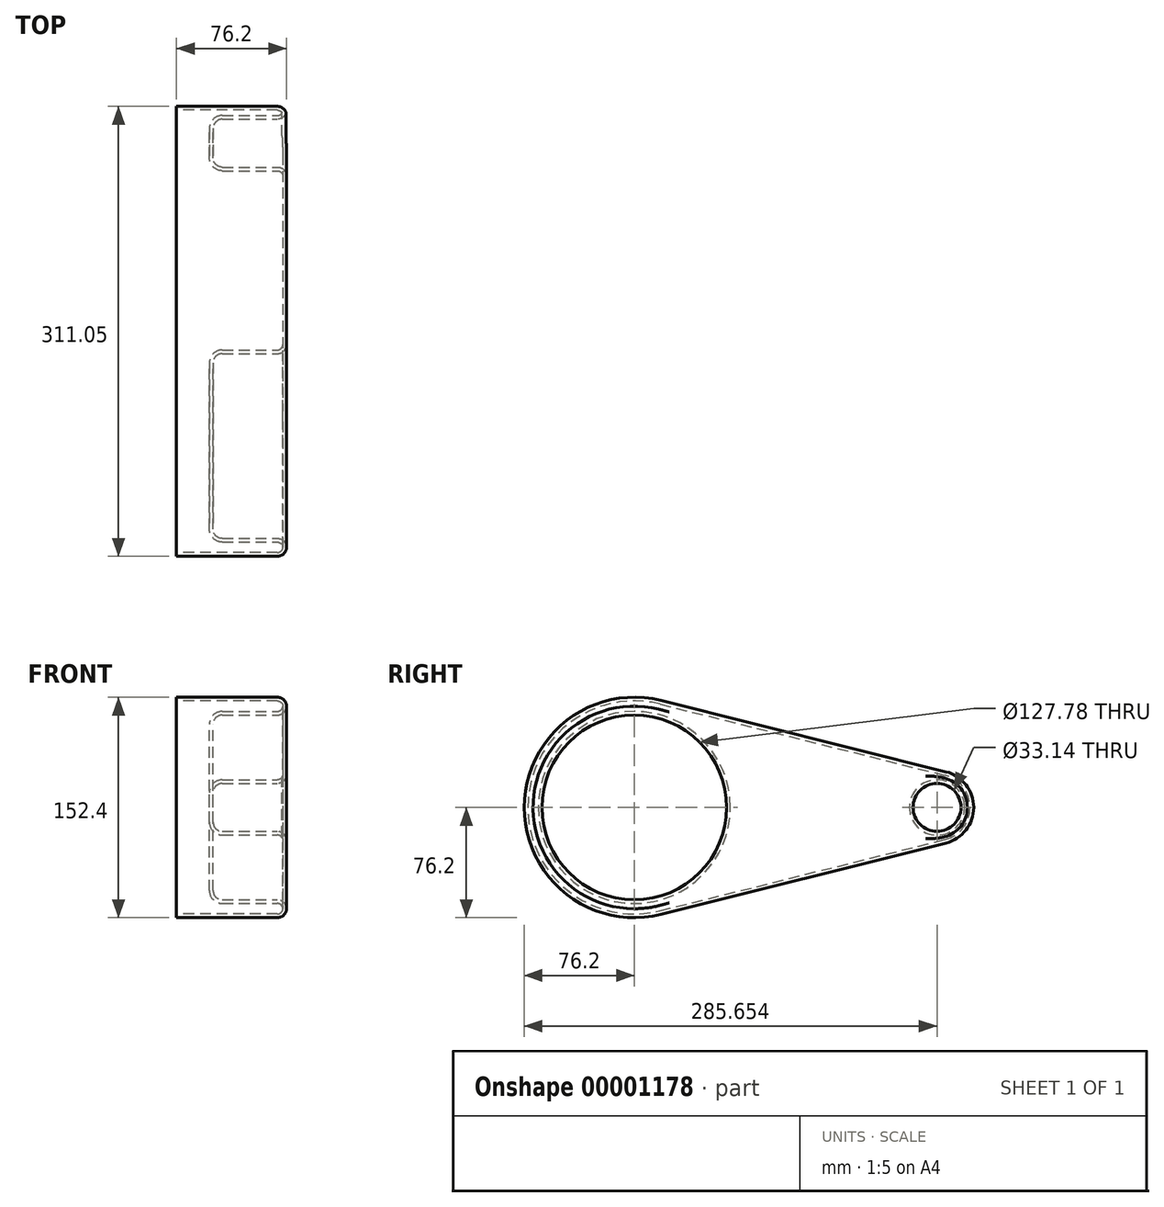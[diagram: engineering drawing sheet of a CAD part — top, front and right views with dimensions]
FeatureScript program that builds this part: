
annotation { "Feature Type Name" : "Feature", "Feature Type Description" : "" }
export const myFeature = defineFeature(function(context is Context, id is Id, definition is map)
    precondition{}
    {
        {
            var Q0;
            Q0=qCreatedBy(makeId("Right.planeOp"),FACE);
            var sketch = newSketch(context, id + "F0", { "sketchPlane" : qUnion([Q0])});
            skCircle(sketch, "E0", {"center": v(0, 0) * mm, "radius": 76.2 * mm});
            skCircle(sketch, "E1", {"center": v(209.45, 0) * mm, "radius": 25.4 * mm});
            skLineSegment(sketch, "E2", {"start": v(18.48, 73.92) * mm, "end": v(215.61, 24.64) * mm});
            skLineSegment(sketch, "E3", {"start": v(18.48, -73.92) * mm, "end": v(215.61, -24.64) * mm});
            skSolve(sketch);
        }
        {
            var Q0;
            {var subQ0=sQuery(id+"F0.wireOp",EDGE,"E1");var subQ2=makeQuery(id+"F0.imprint","INTERSECT",VERTEX,{"derivedFrom":[subQ0,sQuery(id+"F0.wireOp",EDGE,"E2")]});Q0=makeQuery(id+"F0.imprint","IMPRINT",FACE,{"disambiguationData":[TD([[makeQuery(id+"F0.imprint","IMPRINT",EDGE,{"disambiguationData":[TD([[subQ2,-1.0]])],"derivedFrom":subQ0}),1.0]])]});}
            var Q1;
            {var subQ1=sQuery(id+"F0.wireOp",EDGE,"E2");Q1=makeQuery(id+"F0.imprint","IMPRINT",FACE,{"disambiguationData":[TD([[makeQuery(id+"F0.imprint","IMPRINT",EDGE,{"derivedFrom":subQ1}),-1.0]])]});}
            var Q2;
            {var subQ0=sQuery(id+"F0.wireOp",EDGE,"E0");var subQ2=makeQuery(id+"F0.imprint","INTERSECT",VERTEX,{"derivedFrom":[subQ0,sQuery(id+"F0.wireOp",EDGE,"E2")]});Q2=makeQuery(id+"F0.imprint","IMPRINT",FACE,{"disambiguationData":[TD([[makeQuery(id+"F0.imprint","IMPRINT",EDGE,{"disambiguationData":[TD([[subQ2,-1.0]])],"derivedFrom":subQ0}),1.0]])]});}
            extrude(context, id + "F1", {"entities" : qUnion([Q0, Q1, Q2]), "depth" : 76.2 * mm});
        }
        {
            var Q0;
            Q0=makeQuery(id+"F1.opExtrude","CAP_FACE",FACE,{"disambiguationData":[OSD([sQuery(id+"F0.wireOp",EDGE,"E0"),sQuery(id+"F0.wireOp",EDGE,"E1"),sQuery(id+"F0.wireOp",EDGE,"E2"),sQuery(id+"F0.wireOp",EDGE,"E3")])],"isStart":false});
            var sketch = newSketch(context, id + "F2", { "sketchPlane" : qUnion([Q0])});
            skCircle(sketch, "E4", {"center": v(0, 0) * mm, "radius": 63.9 * mm});
            skCircle(sketch, "E5", {"center": v(209.45, 0) * mm, "radius": 16.57 * mm});
            skSolve(sketch);
        }
        {
            var Q0;
            Q0=makeQuery(id+"F2.imprint","IMPRINT",FACE,{"disambiguationData":[TD([[makeQuery(id+"F2.imprint","IMPRINT",EDGE,{"derivedFrom":sQuery(id+"F2.wireOp",EDGE,"E5")}),1.0]])]});
            var Q1;
            Q1=makeQuery(id+"F2.imprint","IMPRINT",FACE,{"disambiguationData":[TD([[makeQuery(id+"F2.imprint","IMPRINT",EDGE,{"derivedFrom":sQuery(id+"F2.wireOp",EDGE,"E4")}),1.0]])]});
            extrude(context, id + "F3", {"entities" : qUnion([Q0, Q1]), "operationType" : NewBodyOperationType.REMOVE, "oppositeDirection" : true, "depth" : 50.8 * mm});
        }
        {
            var Q0;
            Q0=makeQuery(id+"F1.opExtrude","CAP_FACE",FACE,{"disambiguationData":[OSD([sQuery(id+"F0.wireOp",EDGE,"E0"),sQuery(id+"F0.wireOp",EDGE,"E1"),sQuery(id+"F0.wireOp",EDGE,"E2"),sQuery(id+"F0.wireOp",EDGE,"E3")])],"isStart":false});
            var Q1;
            Q1=makeQuery(id+"F3.boolean.opBoolean","COPY",EDGE,{"derivedFrom":makeQuery(id+"F3.opExtrude","CAP_EDGE",EDGE,{"disambiguationData":[OSD([sQuery(id+"F2.wireOp",EDGE,"E4")])],"isStart":false})});
            var Q2;
            Q2=makeQuery(id+"F3.boolean.opBoolean","COPY",EDGE,{"derivedFrom":makeQuery(id+"F3.opExtrude","CAP_EDGE",EDGE,{"disambiguationData":[OSD([sQuery(id+"F2.wireOp",EDGE,"E5")])],"isStart":false})});
            fillet(context, id + "F4", {"entities" : qUnion([Q0, Q1, Q2]), "radius" : 6.35 * mm, "tangentPropagation" : true, "allowEdgeOverflow" : false});
        }
        {
            var Q0;
            Q0=makeQuery(id+"F1.opExtrude","CAP_FACE",FACE,{"disambiguationData":[OSD([sQuery(id+"F0.wireOp",EDGE,"E0"),sQuery(id+"F0.wireOp",EDGE,"E1"),sQuery(id+"F0.wireOp",EDGE,"E2"),sQuery(id+"F0.wireOp",EDGE,"E3")])],"isStart":true});
            shell(context, id + "F5", {"entities" : qUnion([Q0]), "thickness" : 2.54 * mm});
        }
    });
